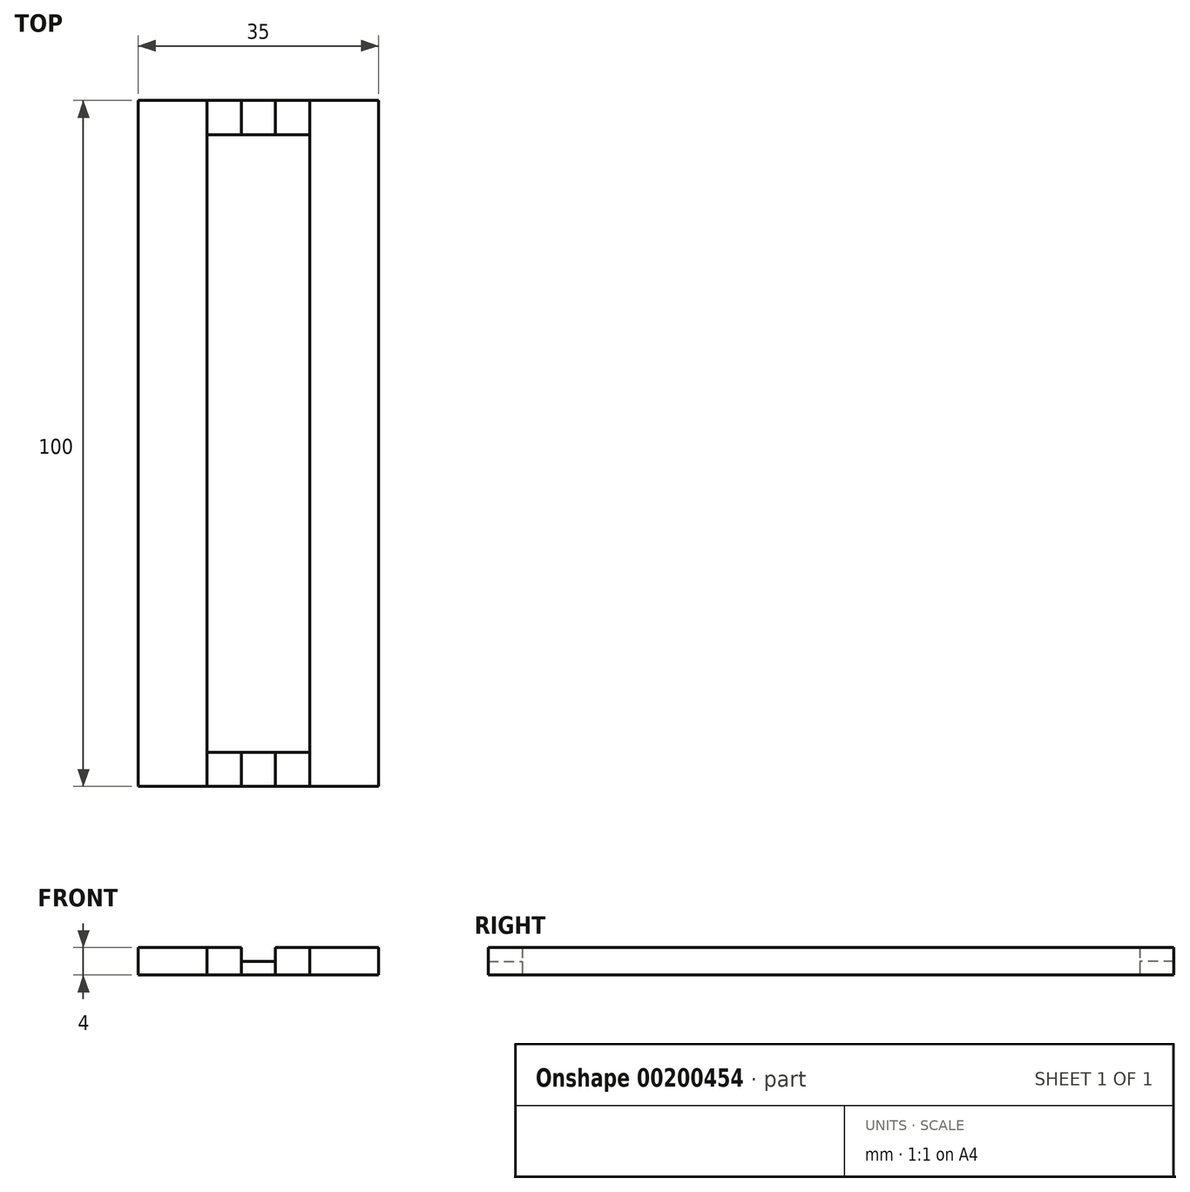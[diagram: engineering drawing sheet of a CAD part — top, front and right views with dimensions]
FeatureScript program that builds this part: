
annotation { "Feature Type Name" : "Feature", "Feature Type Description" : "" }
export const myFeature = defineFeature(function(context is Context, id is Id, definition is map)
    precondition{}
    {
        {
            var Q0;
            Q0=qCreatedBy(makeId("Top.planeOp"),FACE);
            var sketch = newSketch(context, id + "F0", { "sketchPlane" : qUnion([Q0])});
            skLineSegment(sketch, "E0.bottom", {"start": v(0, 0) * mm, "end": v(35, 0) * mm});
            skLineSegment(sketch, "E0.top", {"start": v(0, 100) * mm, "end": v(35, 100) * mm});
            skLineSegment(sketch, "E0.left", {"start": v(0, 0) * mm, "end": v(0, 100) * mm});
            skLineSegment(sketch, "E0.right", {"start": v(35, 0) * mm, "end": v(35, 100) * mm});
            skSolve(sketch);
        }
        {
            var Q0;
            Q0=makeQuery(id+"F0.imprint","IMPRINT",FACE,{"disambiguationData":[TD([[makeQuery(id+"F0.imprint","IMPRINT",EDGE,{"derivedFrom":sQuery(id+"F0.wireOp",EDGE,"E0.bottom")}),1.0]])]});
            var sketch = newSketch(context, id + "F1", { "sketchPlane" : qUnion([Q0])});
            skLineSegment(sketch, "E1.bottom", {"start": v(0, 100) * mm, "end": v(10, 100) * mm});
            skLineSegment(sketch, "E1.top", {"start": v(0, 0) * mm, "end": v(10, 0) * mm});
            skLineSegment(sketch, "E1.left", {"start": v(0, 100) * mm, "end": v(0, 0) * mm});
            skLineSegment(sketch, "E1.right", {"start": v(10, 100) * mm, "end": v(10, 0) * mm});
            skLineSegment(sketch, "E2.bottom", {"start": v(35, 100) * mm, "end": v(25, 100) * mm});
            skLineSegment(sketch, "E2.top", {"start": v(35, 0) * mm, "end": v(25, 0) * mm});
            skLineSegment(sketch, "E2.left", {"start": v(35, 100) * mm, "end": v(35, 0) * mm});
            skLineSegment(sketch, "E2.right", {"start": v(25, 100) * mm, "end": v(25, 0) * mm});
            skSolve(sketch);
        }
        {
            var Q0;
            Q0=makeQuery(id+"F0.imprint","IMPRINT",FACE,{"disambiguationData":[TD([[makeQuery(id+"F0.imprint","IMPRINT",EDGE,{"derivedFrom":sQuery(id+"F0.wireOp",EDGE,"E0.bottom")}),1.0]])]});
            var sketch = newSketch(context, id + "F2", { "sketchPlane" : qUnion([Q0])});
            skLineSegment(sketch, "E3.bottom", {"start": v(15, 100) * mm, "end": v(20, 100) * mm});
            skLineSegment(sketch, "E3.top", {"start": v(15, 95) * mm, "end": v(20, 95) * mm});
            skLineSegment(sketch, "E3.left", {"start": v(15, 100) * mm, "end": v(15, 95) * mm});
            skLineSegment(sketch, "E3.right", {"start": v(20, 100) * mm, "end": v(20, 95) * mm});
            skLineSegment(sketch, "E4.bottom", {"start": v(15, 0) * mm, "end": v(20, 0) * mm});
            skLineSegment(sketch, "E4.top", {"start": v(15, 5) * mm, "end": v(20, 5) * mm});
            skLineSegment(sketch, "E4.left", {"start": v(15, 0) * mm, "end": v(15, 5) * mm});
            skLineSegment(sketch, "E4.right", {"start": v(20, 0) * mm, "end": v(20, 5) * mm});
            skSolve(sketch);
        }
        {
            var Q0;
            Q0=makeQuery(id+"F2.imprint","IMPRINT",FACE,{"disambiguationData":[TD([[makeQuery(id+"F2.imprint","IMPRINT",EDGE,{"derivedFrom":sQuery(id+"F2.wireOp",EDGE,"E3.top")}),-1.0]])]});
            var sketch = newSketch(context, id + "F3", { "sketchPlane" : qUnion([Q0])});
            skLineSegment(sketch, "E5.bottom", {"start": v(10, 100) * mm, "end": v(15, 100) * mm});
            skLineSegment(sketch, "E5.top", {"start": v(10, 95) * mm, "end": v(15, 95) * mm});
            skLineSegment(sketch, "E5.left", {"start": v(10, 100) * mm, "end": v(10, 95) * mm});
            skLineSegment(sketch, "E5.right", {"start": v(15, 100) * mm, "end": v(15, 95) * mm});
            skLineSegment(sketch, "E6.bottom", {"start": v(20, 100) * mm, "end": v(25, 100) * mm});
            skLineSegment(sketch, "E6.top", {"start": v(20, 95) * mm, "end": v(25, 95) * mm});
            skLineSegment(sketch, "E6.left", {"start": v(20, 100) * mm, "end": v(20, 95) * mm});
            skLineSegment(sketch, "E6.right", {"start": v(25, 100) * mm, "end": v(25, 95) * mm});
            skLineSegment(sketch, "E7.bottom", {"start": v(15, 0) * mm, "end": v(10, 0) * mm});
            skLineSegment(sketch, "E7.top", {"start": v(15, 5) * mm, "end": v(10, 5) * mm});
            skLineSegment(sketch, "E7.left", {"start": v(15, 0) * mm, "end": v(15, 5) * mm});
            skLineSegment(sketch, "E7.right", {"start": v(10, 0) * mm, "end": v(10, 5) * mm});
            skLineSegment(sketch, "E8.bottom", {"start": v(25, 0) * mm, "end": v(20, 0) * mm});
            skLineSegment(sketch, "E8.top", {"start": v(25, 5) * mm, "end": v(20, 5) * mm});
            skLineSegment(sketch, "E8.left", {"start": v(25, 0) * mm, "end": v(25, 5) * mm});
            skLineSegment(sketch, "E8.right", {"start": v(20, 0) * mm, "end": v(20, 5) * mm});
            skSolve(sketch);
        }
        {
            var Q0;
            Q0 = qSketchRegion(id + "F1", true);
            extrude(context, id + "F4", {"entities" : qUnion([Q0]), "depth" : 4 * mm});
        }
        {
            var Q0;
            Q0 = qSketchRegion(id + "F3", true);
            extrude(context, id + "F5", {"entities" : qUnion([Q0]), "depth" : 4 * mm});
        }
        {
            var Q0;
            Q0 = qSketchRegion(id + "F2", true);
            extrude(context, id + "F6", {"entities" : qUnion([Q0]), "depth" : 2 * mm});
        }
    });
